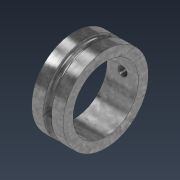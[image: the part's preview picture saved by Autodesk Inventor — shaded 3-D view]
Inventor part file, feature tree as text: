
AUTODESK INVENTOR PART (.ipt)
format: ipt  version: 2022 (Build 260153000, 153)  size: 157,696 bytes
history: native  units: mm
features: sketch x2, revolve x1, extrude x1
ambient origin geometry x8: Origin, YZ Plane, XZ Plane, XY Plane, X Axis, Y Axis, Z Axis, Center Point
bodies: Solid1 (feature_tree)
feature tree (4):
  revolve  "Revolution1"  [1 undecoded]
  extrude  "Extrusion1"  Depth=3.0mm
  sketch  "Sketch1"  dims[d0=200.0mm d1=65.0mm]
  sketch  "Sketch2"  dims[d2=24.0mm d3=3.0mm d4=90.0deg d5=50.0mm d6=7.0mm d7=0.0mm d8=0.0mm]
note: 1 required parameter value undecoded (feature->parameter linkage not recoverable at this tier; creation-order binding heuristic only, values carry confidence <= 0.55)
